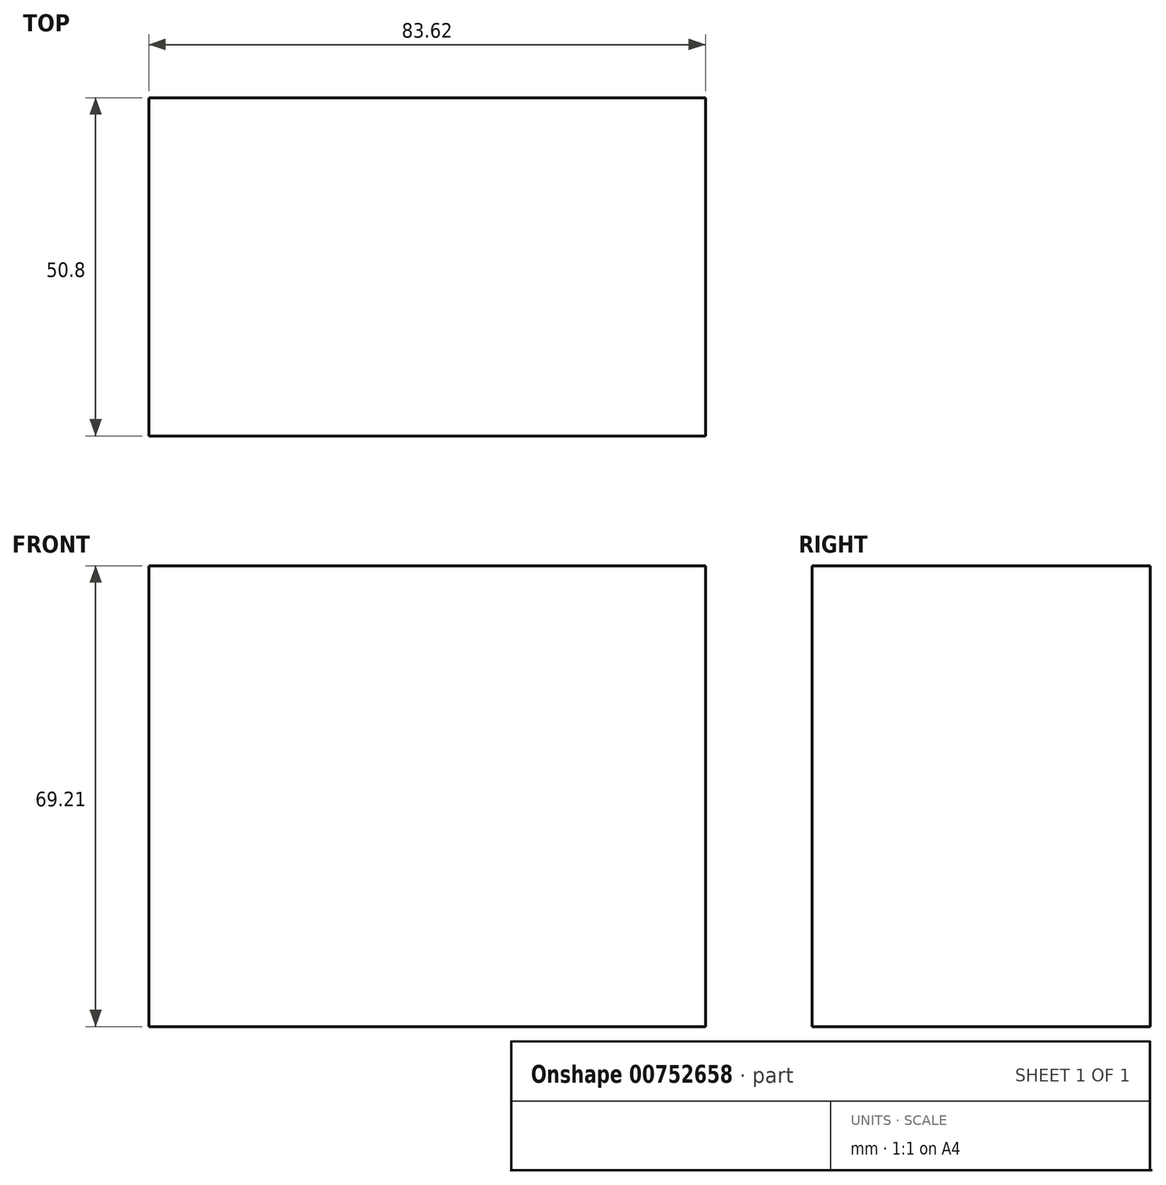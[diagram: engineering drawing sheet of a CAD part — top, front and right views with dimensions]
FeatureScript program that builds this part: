
annotation { "Feature Type Name" : "Feature", "Feature Type Description" : "" }
export const myFeature = defineFeature(function(context is Context, id is Id, definition is map)
    precondition{}
    {
        {
            var Q0;
            Q0=qCreatedBy(makeId("Front.planeOp"),FACE);
            var sketch = newSketch(context, id + "F0", { "sketchPlane" : qUnion([Q0])});
            skLineSegment(sketch, "E0.bottom", {"start": v(-40.4, 42.6) * mm, "end": v(43.2, 42.6) * mm});
            skLineSegment(sketch, "E0.top", {"start": v(-40.4, -26.6) * mm, "end": v(43.2, -26.6) * mm});
            skLineSegment(sketch, "E0.left", {"start": v(-40.4, 42.6) * mm, "end": v(-40.4, -26.6) * mm});
            skLineSegment(sketch, "E0.right", {"start": v(43.2, 42.6) * mm, "end": v(43.2, -26.6) * mm});
            skSolve(sketch);
        }
        {
            var Q0;
            Q0=sQuery(id+"F0.wireOp",EDGE,"E0.bottom");
            var Q1;
            Q1=sQuery(id+"F0.wireOp",EDGE,"E0.left");
            var Q2;
            Q2=sQuery(id+"F0.wireOp",EDGE,"E0.top");
            var Q3;
            Q3=sQuery(id+"F0.wireOp",EDGE,"E0.right");
            extrude(context, id + "F1", {"bodyType" : ToolBodyType.SURFACE, "surfaceEntities" : qUnion([Q0, Q1, Q2, Q3]), "depth" : 50.8 * mm, "offsetDistance" : 25.4 * mm});
        }
    });
